# Revit family: SH-20.16
name_source: partatom
category: Устройства связи
revit_build: Autodesk Revit 2016 (Build: 20160314_0715(x64)
units: mm (PartAtom-declared; Revit-internal decimal feet)

## family parameters
Всегда вертикально = Нет
На основе рабочей плоскости = Да
Общий = Да
При загрузке вырезать с полостями = Нет
Размер круглого соединителя = Использовать диаметр
Сохранять ориентацию аннотаций = Нет
Тип детали = Нормальный
Точка расчета площади = Нет

## types (3) — shared parameters
ADSK_URL страницы изделия = https://www.bas-ip.ru
ADSK_Версия Revit = Revit 2016
ADSK_Единица измерения = шт
ADSK_Завод-изготовитель = BAS-IP
ADSK_Классификация нагрузок = Коммутатор
ADSK_Количество фаз = 1
ADSK_Коэффициент мощности = 0.9
ADSK_Напряжение = 48 В
ADSK_Номинальная мощность = 290 Вт
ADSK_Полная мощность = 322 В·А
BIM library = https://bimlib.ru
URL = https://www.bas-ip.ru
Группа модели = Коммутатор
Изготовитель = BAS-IP
Изображение типоразмера = <Нет>
Количество портов UpLink = 2 порта 10/100Base-TX
Максимальная длина кабеля при подключении к портам с PoE = 100 метров
Метод подачи питания на портах с PoE = Метод B
Описание = Неуправляемый PoE коммутатор 10/100Base-TX, предназначенный для подключения сетевых устройств поддерживающих технологию Power over Ethernet.
Уровень коммутатора = 1 (неуправляемый)
zero-valued in all types: Отметка по умолчанию

## per-type parameters (varying)
| type | ADSK_Наименование | ADSK_Размер_Длина | ADSK_Размер_Толщина | ADSK_Размер_Ширина | Габаритные размеры | Источник питания | Количество портов PoE | Максимальная мощность на каждом порту с PoE |
| SH-20.4 | POE КОММУТАТОР SH-20.4 | 150 мм | 29 мм | 77 мм | 150х77х28,5 мм | Внешний 48 В 1,25 А (в комплекте) | PoE 4 порта IEEE 802.3af | 15 Вт |
| SH-20.8 | POE КОММУТАТОР SH-20.8 | 190 мм | 29 мм | 77 мм | 190х77х28,5 мм | Внешний 48 В 3,0 А (в комплекте) | PoE 8 порта IEEE 802.3af | 15.4 Вт |
| SH-20.16 | POE КОММУТАТОР SH-20.16 | 330 мм | 45 мм | 205 мм | 330х205х44,5 мм |  | PoE 16 порта IEEE 802.3af | 15.4 Вт |

note: column(s) folded — value = type name in every type: ADSK_Марка, ADSK_Наименование краткое
